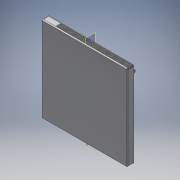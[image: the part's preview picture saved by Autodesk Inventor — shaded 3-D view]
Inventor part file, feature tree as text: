
AUTODESK INVENTOR PART (.ipt)
format: ipt  version: 2018 (Build 220112000, 112)  size: 473,600 bytes
history: native  units: in
note: dims shown in document units (in); Inventor stores cm internally (conversion verified against a paired STEP export)
features: reference x11, sketch x8, extrude x8, fillet x8, plane x3, other x3, thread x2, mirror x1
ambient origin geometry x8: Origin, YZ Plane, XZ Plane, XY Plane, X Axis, Y Axis, Z Axis, Center Point
bodies: Solid1 (feature_tree)
feature tree (44):
  sketch  "Sketch1"  dims[d0=1.0in d1=0.0in d2=0.2in d3=0.0in]
  plane  "Work Plane1"
  extrude  "Extrusion1"  Depth=0.2in TaperAngle=0.0deg
  extrude  "Extrusion2"  Depth=0.25in
  sketch  "Sketch3"  dims[d7=0.175in d8=0.175in]
  plane  "Work Plane2"
  extrude  "Extrusion3"  Depth=0.175in
  extrude  "Extrusion4"  Depth=0.025in
  fillet  "Fillet1"  Radius=0.1in
  fillet  "Fillet2"  Radius=0.1in
  thread  "Thread1"  [1 undecoded]
  plane  "Work Plane3"
  mirror  "Mirror1"
  fillet  "Fillet3"  Radius=1.0in
  fillet  "Fillet4"  Radius=0.1in
  thread  "Thread2"  [1 undecoded]
  extrude  "Extrusion5"  Depth=0.175in
  fillet  "Fillet5"  Radius=0.0875in
  fillet  "Fillet6"  Radius=0.0875in
  extrude  "Extrusion6"  Depth=0.1in TaperAngle=0.0deg
  fillet  "Fillet7"  Radius=0.1in
  extrude  "Extrusion7"  Depth=0.1in TaperAngle=0.0deg
  fillet  "Fillet8"  Radius=0.05in
  extrude  "Extrusion8"  Depth=0.025in
  reference  "Reference1"
  sketch  "Sketch2"  dims[d4=0.2in d5=0.0in d6=0.25in]
  reference  "Reference2"
  reference  "Reference3"
  reference  "Reference4"
  reference  "Reference5"
  reference  "Reference6"
  reference  "Reference7"
  reference  "Reference8"
  reference  "Reference9"
  reference  "Reference10"
  sketch  "Sketch4"  dims[d9=0.125in d10=0.0925in d11=0.1in d12=0.0in d13=0.1in d14=0.025in d15=1.0in d16=0.0in d17=0.1in d18=0.025in]
  reference  "Reference11"
  sketch  "Sketch5"  dims[d19=1.0in d20=0.0in d21=0.175in d22=0.0875in d23=0.0875in]
  sketch  "Sketch6"  dims[d24=0.125in d25=0.1in d26=0.0in d27=0.1in]
  sketch  "Sketch7"  dims[d28=0.025in d29=0.1in d30=0.0in d31=0.05in]
  sketch  "Sketch8"  dims[d33=0.75in d34=0.025in d35=0.025in d36=0.025in d37=0.025in d38=0.025in d39=0.025in d40=0.025in d41=0.025in d42=0.025in d43=0.025in d44=0.025in d45=0.025in d46=0.0in d47=0.05in d48=0.025in d49=0.025in d50=0.001in d51=0.0in]
  other  "<userpath>\Documents\Commodore Cube Project\Case\Assembly.iam"
  other  "Assembly.iam"
  other  "Tray:1"
note: 2 required parameter values undecoded (feature->parameter linkage not recoverable at this tier; creation-order binding heuristic only, values carry confidence <= 0.55)
